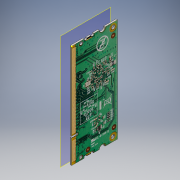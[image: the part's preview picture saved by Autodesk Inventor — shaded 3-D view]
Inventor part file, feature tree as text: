
AUTODESK INVENTOR PART (.ipt)
format: ipt  version: 2016 (Build 200138000, 138)  size: 4,615,680 bytes
history: native  units: mm
features: sketch x9, other x9, extrude x4, plane x1
ambient origin geometry x8: Origin, YZ Plane, XZ Plane, XY Plane, X Axis, Y Axis, Z Axis, Center Point
bodies: Solid1 (feature_tree)
feature tree (23):
  extrude  "Extrusion1"  Depth=67.6mm
  sketch  "Sketch2"  dims[d2=1.0mm d3=0.0mm d5=2.5mm]
  sketch  "Sketch3"  dims[d6=2.5mm d7=3.75mm]
  extrude  "Extrusion2"  Depth=1.0mm
  extrude  "Extrusion3"  Depth=3.75mm
  sketch  "Sketch6"  dims[d8=3.75mm d9=2.0mm]
  extrude  "Extrusion4"  Depth=2.0mm
  other  "Decal3"
  plane  "Work Plane1"
  other  "Decal4"
  other  "Decal5"
  other  "Decal6"
  sketch  "Sketch1"  dims[d0=30.0mm d1=67.6mm]
  other  "Image1"
  sketch  "Sketch8"  dims[d10=2.0mm]
  other  "Image4"
  sketch  "Sketch9"  dims[d11=1.0mm d12=0.0mm]
  sketch  "Sketch14"  dims[d13=1.0mm d14=0.0mm]
  other  "Image5"
  sketch  "Sketch15"  dims[d23=67.6mm]
  other  "Image6"
  sketch  "Sketch16"  dims[d27=0.5mm d28=0.0mm d30=5.0mm d32=67.6mm d37=67.6mm d42=67.6mm]
  other  "Image7"
